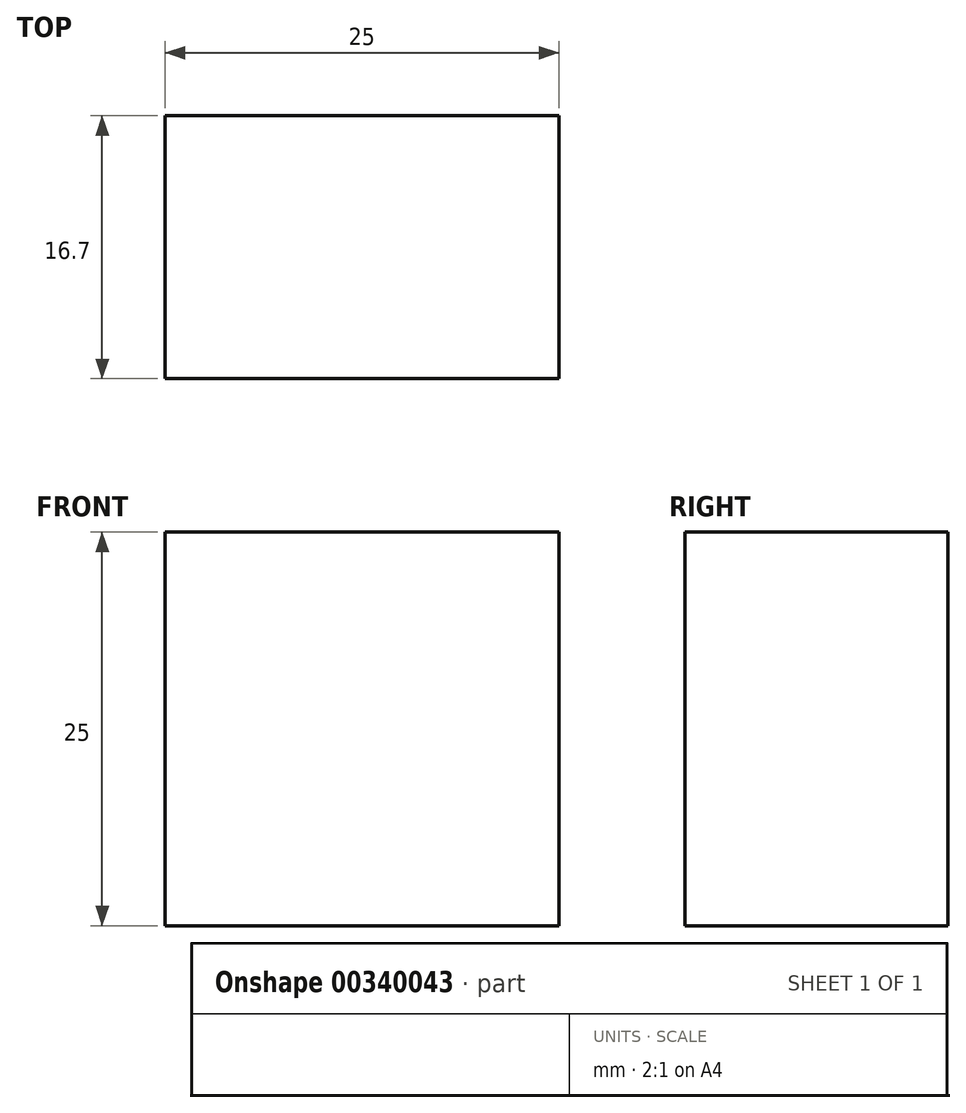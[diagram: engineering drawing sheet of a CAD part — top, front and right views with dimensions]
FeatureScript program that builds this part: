
annotation { "Feature Type Name" : "Feature", "Feature Type Description" : "" }
export const myFeature = defineFeature(function(context is Context, id is Id, definition is map)
    precondition{}
    {
        {
            var Q0;
            Q0=qCreatedBy(makeId("Front.planeOp"),FACE);
            var sketch = newSketch(context, id + "F0", { "sketchPlane" : qUnion([Q0])});
            skLineSegment(sketch, "E0.bottom", {"start": v(-12.9, 12.65) * mm, "end": v(12.1, 12.65) * mm});
            skLineSegment(sketch, "E0.top", {"start": v(-12.9, -12.35) * mm, "end": v(12.1, -12.35) * mm});
            skLineSegment(sketch, "E0.left", {"start": v(-12.9, 12.65) * mm, "end": v(-12.9, -12.35) * mm});
            skLineSegment(sketch, "E0.right", {"start": v(12.1, 12.65) * mm, "end": v(12.1, -12.35) * mm});
            skSolve(sketch);
        }
        {
            var Q0;
            Q0=qSketchRegion(id+"F0",true);
            extrude(context, id + "F1", {"entities" : qUnion([Q0]), "depth" : 16.7 * mm});
        }
    });
